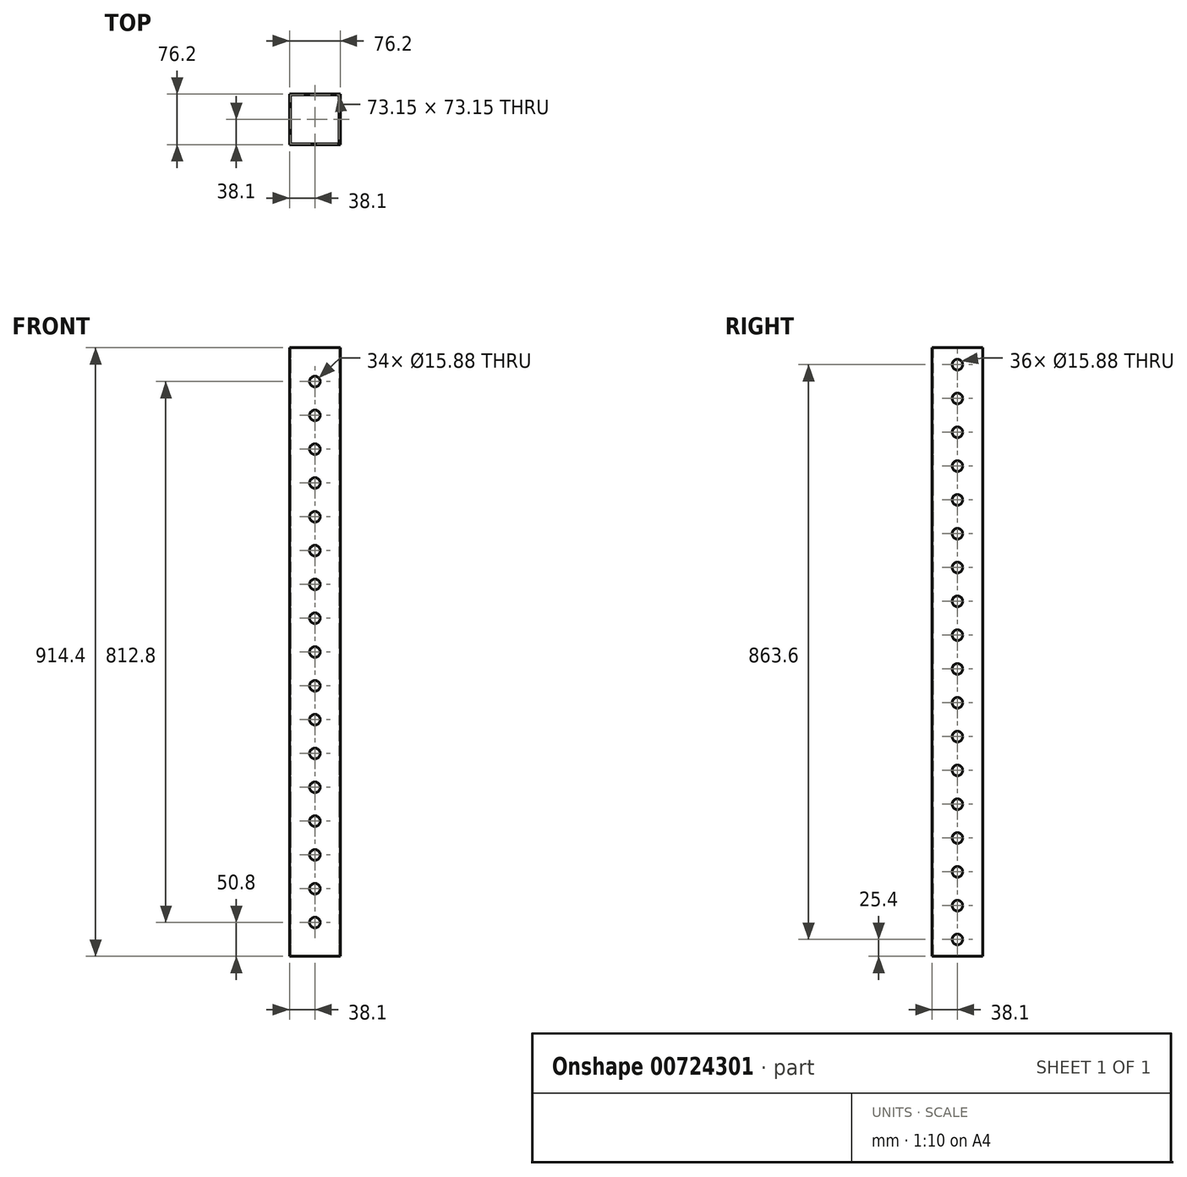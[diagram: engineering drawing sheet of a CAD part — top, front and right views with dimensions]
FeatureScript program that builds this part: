
annotation { "Feature Type Name" : "Feature", "Feature Type Description" : "" }
export const myFeature = defineFeature(function(context is Context, id is Id, definition is map)
    precondition{}
    {
        {
            var Q0;
            Q0=qCreatedBy(makeId("Top.planeOp"),FACE);
            var sketch = newSketch(context, id + "F0", { "sketchPlane" : qUnion([Q0])});
            skLineSegment(sketch, "E0.bottom", {"start": v(-38.1, -38.1) * mm, "end": v(38.1, -38.1) * mm});
            skLineSegment(sketch, "E0.top", {"start": v(-38.1, 38.1) * mm, "end": v(38.1, 38.1) * mm});
            skLineSegment(sketch, "E0.left", {"start": v(-38.1, -38.1) * mm, "end": v(-38.1, 38.1) * mm});
            skLineSegment(sketch, "E0.right", {"start": v(38.1, -38.1) * mm, "end": v(38.1, 38.1) * mm});
            skPoint(sketch, "E0.middle", {"position": v(0, 0) * mm});
            skLineSegment(sketch, "E1.bottom", {"start": v(-36.58, -36.58) * mm, "end": v(36.58, -36.58) * mm});
            skLineSegment(sketch, "E1.top", {"start": v(-36.58, 36.58) * mm, "end": v(36.58, 36.58) * mm});
            skLineSegment(sketch, "E1.left", {"start": v(-36.58, -36.58) * mm, "end": v(-36.58, 36.58) * mm});
            skLineSegment(sketch, "E1.right", {"start": v(36.58, -36.58) * mm, "end": v(36.58, 36.58) * mm});
            skSolve(sketch);
        }
        {
            var Q0;
            Q0=makeQuery(id+"F0.imprint","IMPRINT",FACE,{"disambiguationData":[TD([[makeQuery(id+"F0.imprint","IMPRINT",EDGE,{"derivedFrom":sQuery(id+"F0.wireOp",EDGE,"E0.bottom")}),1.0]])]});
            extrude(context, id + "F1", {"entities" : qUnion([Q0]), "depth" : 914.4 * mm, "offsetDistance" : 25.4 * mm});
        }
        {
            var Q0;
            Q0=qCreatedBy(makeId("Front.planeOp"),FACE);
            cPlane(context, id + "F2", {"entities" : qUnion([Q0]), "cplaneType" : CPlaneType.OFFSET, "offset" : 76.2 * mm, "width" : 152.4 * mm, "height" : 152.4 * mm});
        }
        {
            var Q0;
            Q0=qCreatedBy(id+"F2.planeOp",FACE);
            var sketch = newSketch(context, id + "F3", { "sketchPlane" : qUnion([Q0])});
            skPoint(sketch, "E2", {"position": v(0, 50.8) * mm});
            skPoint(sketch, "E3.1.0.0", {"position": v(0, 101.6) * mm});
            skPoint(sketch, "E3.2.0.0", {"position": v(0, 152.4) * mm});
            skPoint(sketch, "E3.3.0.0", {"position": v(0, 203.2) * mm});
            skPoint(sketch, "E3.4.0.0", {"position": v(0, 254) * mm});
            skPoint(sketch, "E3.5.0.0", {"position": v(0, 304.8) * mm});
            skPoint(sketch, "E3.6.0.0", {"position": v(0, 355.6) * mm});
            skPoint(sketch, "E3.7.0.0", {"position": v(0, 406.4) * mm});
            skPoint(sketch, "E3.8.0.0", {"position": v(0, 457.2) * mm});
            skPoint(sketch, "E3.9.0.0", {"position": v(0, 508) * mm});
            skPoint(sketch, "E3.10.0.0", {"position": v(0, 558.8) * mm});
            skPoint(sketch, "E3.11.0.0", {"position": v(0, 609.6) * mm});
            skPoint(sketch, "E3.12.0.0", {"position": v(0, 660.4) * mm});
            skPoint(sketch, "E3.13.0.0", {"position": v(0, 711.2) * mm});
            skPoint(sketch, "E3.14.0.0", {"position": v(0, 762) * mm});
            skPoint(sketch, "E3.15.0.0", {"position": v(0, 812.8) * mm});
            skPoint(sketch, "E3.16.0.0", {"position": v(0, 863.6) * mm});
            skLineSegment(sketch, "E3.direction1", {"start": v(0, 50.8) * mm, "end": v(0, 101.6) * mm, "construction": true});
            skSolve(sketch);
        }
        {
            var Q0;
            Q0=qCreatedBy(makeId("Right.planeOp"),FACE);
            cPlane(context, id + "F4", {"entities" : qUnion([Q0]), "cplaneType" : CPlaneType.OFFSET, "offset" : 76.2 * mm, "width" : 152.4 * mm, "height" : 152.4 * mm});
        }
        {
            var Q0;
            Q0=qCreatedBy(id+"F4.planeOp",FACE);
            var sketch = newSketch(context, id + "F5", { "sketchPlane" : qUnion([Q0])});
            skPoint(sketch, "E4", {"position": v(0, 25.4) * mm});
            skPoint(sketch, "E5.1.0.0", {"position": v(0, 76.2) * mm});
            skPoint(sketch, "E5.2.0.0", {"position": v(0, 127) * mm});
            skPoint(sketch, "E5.3.0.0", {"position": v(0, 177.8) * mm});
            skPoint(sketch, "E5.4.0.0", {"position": v(0, 228.6) * mm});
            skPoint(sketch, "E5.5.0.0", {"position": v(0, 279.4) * mm});
            skPoint(sketch, "E5.6.0.0", {"position": v(0, 330.2) * mm});
            skPoint(sketch, "E5.7.0.0", {"position": v(0, 381) * mm});
            skPoint(sketch, "E5.8.0.0", {"position": v(0, 431.8) * mm});
            skPoint(sketch, "E5.9.0.0", {"position": v(0, 482.6) * mm});
            skPoint(sketch, "E5.10.0.0", {"position": v(0, 533.4) * mm});
            skPoint(sketch, "E5.11.0.0", {"position": v(0, 584.2) * mm});
            skPoint(sketch, "E5.12.0.0", {"position": v(0, 635) * mm});
            skPoint(sketch, "E5.13.0.0", {"position": v(0, 685.8) * mm});
            skPoint(sketch, "E5.14.0.0", {"position": v(0, 736.6) * mm});
            skPoint(sketch, "E5.15.0.0", {"position": v(0, 787.4) * mm});
            skPoint(sketch, "E5.16.0.0", {"position": v(0, 838.2) * mm});
            skPoint(sketch, "E5.17.0.0", {"position": v(0, 889) * mm});
            skLineSegment(sketch, "E5.direction1", {"start": v(0, 25.4) * mm, "end": v(0, 76.2) * mm, "construction": true});
            skSolve(sketch);
        }
        {
            var Q0;
            Q0=sQuery(id+"F5.wireOp",VERTEX,"E4");
            var Q1;
            Q1=sQuery(id+"F5.wireOp",VERTEX,"E5.1.0.0");
            var Q2;
            Q2=sQuery(id+"F5.wireOp",VERTEX,"E5.2.0.0");
            var Q3;
            Q3=sQuery(id+"F5.wireOp",VERTEX,"E5.3.0.0");
            var Q4;
            Q4=sQuery(id+"F5.wireOp",VERTEX,"E5.4.0.0");
            var Q5;
            Q5=sQuery(id+"F5.wireOp",VERTEX,"E5.5.0.0");
            var Q6;
            Q6=sQuery(id+"F5.wireOp",VERTEX,"E5.6.0.0");
            var Q7;
            Q7=sQuery(id+"F5.wireOp",VERTEX,"E5.7.0.0");
            var Q8;
            Q8=sQuery(id+"F5.wireOp",VERTEX,"E5.8.0.0");
            var Q9;
            Q9=sQuery(id+"F5.wireOp",VERTEX,"E5.9.0.0");
            var Q10;
            Q10=sQuery(id+"F5.wireOp",VERTEX,"E5.10.0.0");
            var Q11;
            Q11=sQuery(id+"F5.wireOp",VERTEX,"E5.11.0.0");
            var Q12;
            Q12=sQuery(id+"F5.wireOp",VERTEX,"E5.12.0.0");
            var Q13;
            Q13=sQuery(id+"F5.wireOp",VERTEX,"E5.13.0.0");
            var Q14;
            Q14=sQuery(id+"F5.wireOp",VERTEX,"E5.14.0.0");
            var Q15;
            Q15=sQuery(id+"F5.wireOp",VERTEX,"E5.15.0.0");
            var Q16;
            Q16=sQuery(id+"F5.wireOp",VERTEX,"E5.16.0.0");
            var Q17;
            Q17=sQuery(id+"F5.wireOp",VERTEX,"E5.17.0.0");
            var Q18;
            Q18=sQuery(id+"F3.wireOp",VERTEX,"E3.16.0.0");
            var Q19;
            Q19=sQuery(id+"F3.wireOp",VERTEX,"E3.15.0.0");
            var Q20;
            Q20=sQuery(id+"F3.wireOp",VERTEX,"E3.14.0.0");
            var Q21;
            Q21=sQuery(id+"F3.wireOp",VERTEX,"E3.13.0.0");
            var Q22;
            Q22=sQuery(id+"F3.wireOp",VERTEX,"E3.12.0.0");
            var Q23;
            Q23=sQuery(id+"F3.wireOp",VERTEX,"E3.11.0.0");
            var Q24;
            Q24=sQuery(id+"F3.wireOp",VERTEX,"E3.10.0.0");
            var Q25;
            Q25=sQuery(id+"F3.wireOp",VERTEX,"E3.9.0.0");
            var Q26;
            Q26=sQuery(id+"F3.wireOp",VERTEX,"E3.8.0.0");
            var Q27;
            Q27=sQuery(id+"F3.wireOp",VERTEX,"E3.7.0.0");
            var Q28;
            Q28=sQuery(id+"F3.wireOp",VERTEX,"E3.6.0.0");
            var Q29;
            Q29=sQuery(id+"F3.wireOp",VERTEX,"E3.5.0.0");
            var Q30;
            Q30=sQuery(id+"F3.wireOp",VERTEX,"E3.4.0.0");
            var Q31;
            Q31=sQuery(id+"F3.wireOp",VERTEX,"E3.3.0.0");
            var Q32;
            Q32=sQuery(id+"F3.wireOp",VERTEX,"E3.2.0.0");
            var Q33;
            Q33=sQuery(id+"F3.wireOp",VERTEX,"E3.1.0.0");
            var Q34;
            Q34=sQuery(id+"F3.wireOp",VERTEX,"E2");
            var Q35;
            Q35=makeQuery(id+"F1.opExtrude","SWEPT_BODY",BODY,{"disambiguationData":[OSD([sQuery(id+"F0.wireOp",EDGE,"E0.bottom"),sQuery(id+"F0.wireOp",EDGE,"E0.top"),sQuery(id+"F0.wireOp",EDGE,"E0.left"),sQuery(id+"F0.wireOp",EDGE,"E0.right"),sQuery(id+"F0.wireOp",EDGE,"E1.bottom"),sQuery(id+"F0.wireOp",EDGE,"E1.top"),sQuery(id+"F0.wireOp",EDGE,"E1.left"),sQuery(id+"F0.wireOp",EDGE,"E1.right")])]});
            hole(context, id + "F6", {"style" : HoleStyle.SIMPLE, "endStyle" : HoleEndStyle.THROUGH, "holeDiameter" : 15.88 * mm, "majorDiameter" : 6.35 * mm, "isTappedThrough" : true, "tappedDepth" : 12.7 * mm, "tapClearance" : 3, "locations" : qUnion([Q0, Q1, Q2, Q3, Q4, Q5, Q6, Q7, Q8, Q9, Q10, Q11, Q12, Q13, Q14, Q15, Q16, Q17, Q18, Q19, Q20, Q21, Q22, Q23, Q24, Q25, Q26, Q27, Q28, Q29, Q30, Q31, Q32, Q33, Q34]), "scope" : qUnion([Q35])});
        }
    });
